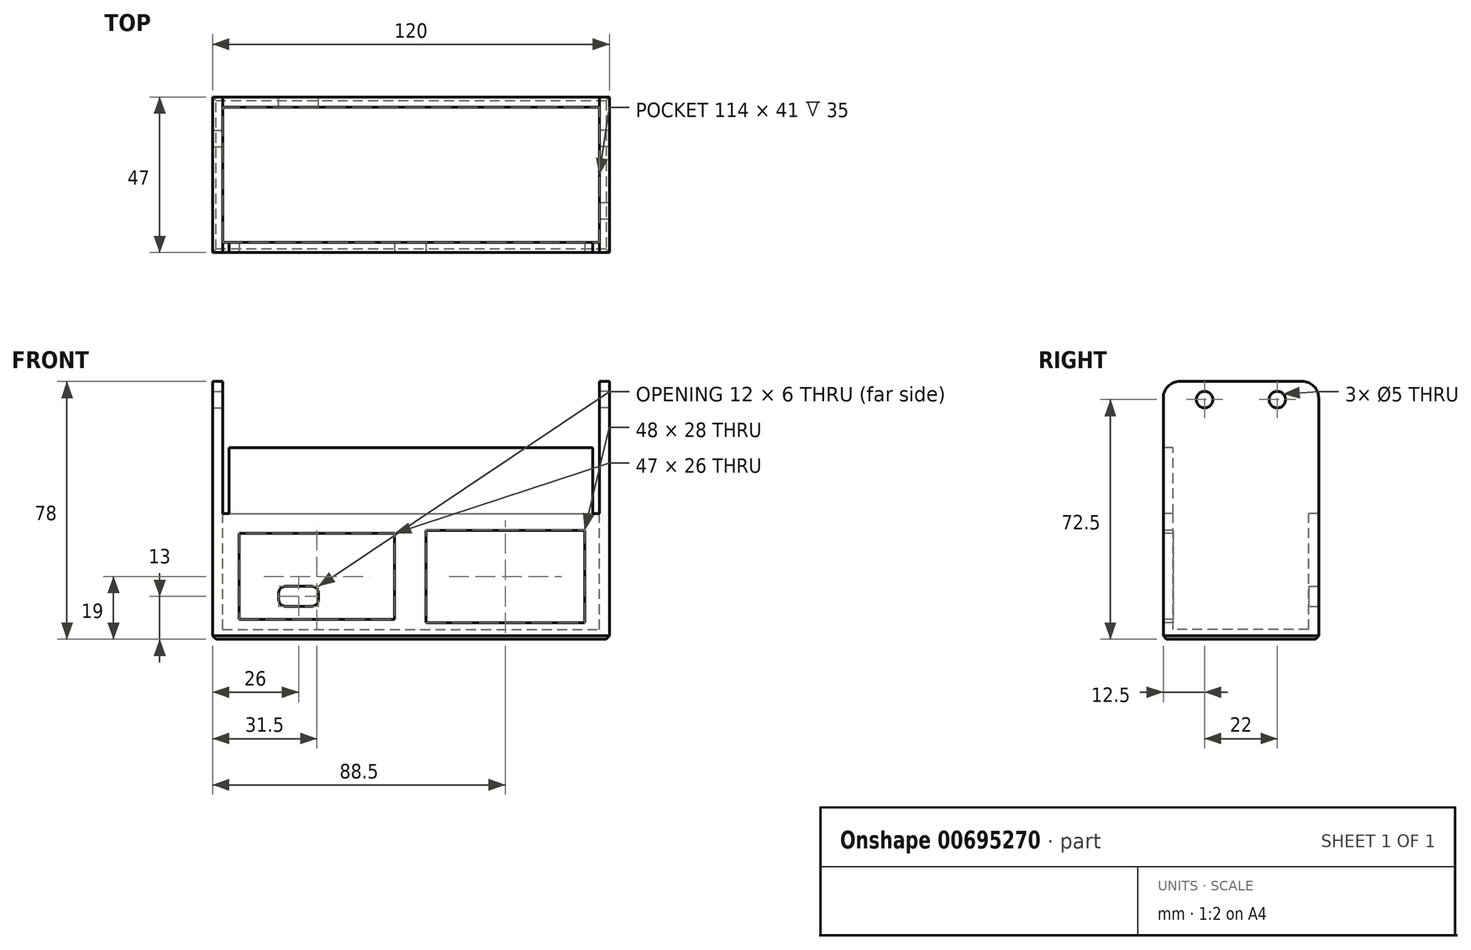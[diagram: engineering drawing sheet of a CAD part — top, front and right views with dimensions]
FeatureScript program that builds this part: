
annotation { "Feature Type Name" : "Feature", "Feature Type Description" : "" }
export const myFeature = defineFeature(function(context is Context, id is Id, definition is map)
    precondition{}
    {
        {
            assignVariable(context, id + "F0", {"name" : "wall", "anyValue" : 3});
        }
        {
            assignVariable(context, id + "F1", {"name" : "width", "anyValue" : 114});
        }
        {
            var Q0;
            Q0=qCreatedBy(makeId("Right.planeOp"),FACE);
            var sketch = newSketch(context, id + "F2", { "sketchPlane" : qUnion([Q0])});
            skLineSegment(sketch, "E0.bottom", {"start": v(17.5, 40) * mm, "end": v(-19.5, 40) * mm});
            skLineSegment(sketch, "E0.top", {"start": v(22.5, -38) * mm, "end": v(-24.5, -38) * mm});
            skLineSegment(sketch, "E0.left", {"start": v(22.5, 35) * mm, "end": v(22.5, -38) * mm});
            skLineSegment(sketch, "E0.right", {"start": v(-24.5, 35) * mm, "end": v(-24.5, -38) * mm});
            skCircle(sketch, "E1", {"center": v(10, 34.5) * mm, "radius": 2.5 * mm});
            skCircle(sketch, "E2", {"center": v(-12, 34.5) * mm, "radius": 2.5 * mm});
            skPoint(sketch, "E3.visualSharp", {"position": v(-24.5, 40) * mm});
            skArc(sketch, "E3.filletArc", {"start": v(-19.5, 40) * mm, "mid": v(-23.04, 38.54) * mm, "end": v(-24.5, 35) * mm});
            skPoint(sketch, "E4.visualSharp", {"position": v(22.5, 40) * mm});
            skArc(sketch, "E4.filletArc", {"start": v(22.5, 35) * mm, "mid": v(21.04, 38.54) * mm, "end": v(17.5, 40) * mm});
            skSolve(sketch);
        }
        {
            var Q0;
            Q0=qSketchRegion(id+"F2",true);
            extrude(context, id + "F3", {"entities" : qUnion([Q0]), "depth" : (getVariable(context, 'wall')) * mm, "offsetDistance" : 25 * mm});
        }
        {
            var Q0;
            Q0=qCreatedBy(makeId("Right.planeOp"),FACE);
            var sketch = newSketch(context, id + "F4", { "sketchPlane" : qUnion([Q0])});
            skLineSegment(sketch, "E5.bottom", {"start": v(22.5, -38) * mm, "end": v(-24.5, -38) * mm});
            skLineSegment(sketch, "E5.top", {"start": v(22.5, -35) * mm, "end": v(-24.5, -35) * mm});
            skLineSegment(sketch, "E5.left", {"start": v(22.5, -38) * mm, "end": v(22.5, -35) * mm});
            skLineSegment(sketch, "E5.right", {"start": v(-24.5, -38) * mm, "end": v(-24.5, -35) * mm});
            skLineSegment(sketch, "E6.bottom", {"start": v(-24.5, -38) * mm, "end": v(-21.5, -38) * mm});
            skLineSegment(sketch, "E6.top", {"start": v(-24.5, 0) * mm, "end": v(-21.5, 0) * mm});
            skLineSegment(sketch, "E6.left", {"start": v(-24.5, -38) * mm, "end": v(-24.5, 0) * mm});
            skLineSegment(sketch, "E6.right", {"start": v(-21.5, -38) * mm, "end": v(-21.5, 0) * mm});
            skLineSegment(sketch, "E7.bottom", {"start": v(22.5, -38) * mm, "end": v(19.5, -38) * mm});
            skLineSegment(sketch, "E7.top", {"start": v(22.5, 0) * mm, "end": v(19.5, 0) * mm});
            skLineSegment(sketch, "E7.left", {"start": v(22.5, -38) * mm, "end": v(22.5, 0) * mm});
            skLineSegment(sketch, "E7.right", {"start": v(19.5, -38) * mm, "end": v(19.5, 0) * mm});
            skSolve(sketch);
        }
        {
            var Q0;
            Q0=qSketchRegion(id+"F4",true);
            extrude(context, id + "F5", {"entities" : qUnion([Q0]), "operationType" : NewBodyOperationType.ADD, "oppositeDirection" : true, "depth" : (getVariable(context, 'width')) * mm, "offsetDistance" : 25 * mm});
        }
        {
            var Q0;
            Q0=makeQuery(id+"F5.opExtrude","CAP_FACE",FACE,{"disambiguationData":[OSD([sQuery(id+"F4.wireOp",EDGE,"E5.bottom"),sQuery(id+"F4.wireOp",EDGE,"E5.top"),sQuery(id+"F4.wireOp",EDGE,"E6.bottom"),sQuery(id+"F4.wireOp",EDGE,"E6.top"),sQuery(id+"F4.wireOp",EDGE,"E6.left"),sQuery(id+"F4.wireOp",EDGE,"E6.right"),sQuery(id+"F4.wireOp",EDGE,"E7.bottom"),sQuery(id+"F4.wireOp",EDGE,"E7.top"),sQuery(id+"F4.wireOp",EDGE,"E7.left"),sQuery(id+"F4.wireOp",EDGE,"E7.right")])],"isStart":false});
            var sketch = newSketch(context, id + "F6", { "sketchPlane" : qUnion([Q0])});
            skLineSegment(sketch, "E8.bottom", {"start": v(19.5, 40) * mm, "end": v(-17.5, 40) * mm});
            skLineSegment(sketch, "E8.top", {"start": v(24.5, -38) * mm, "end": v(-22.5, -38) * mm});
            skLineSegment(sketch, "E8.left", {"start": v(24.5, 35) * mm, "end": v(24.5, -38) * mm});
            skLineSegment(sketch, "E8.right", {"start": v(-22.5, 35) * mm, "end": v(-22.5, -38) * mm});
            skCircle(sketch, "E9", {"center": v(-10, 34.5) * mm, "radius": 2.5 * mm});
            skPoint(sketch, "E10.visualSharp", {"position": v(-22.5, 40) * mm});
            skArc(sketch, "E10.filletArc", {"start": v(-17.5, 40) * mm, "mid": v(-21.04, 38.54) * mm, "end": v(-22.5, 35) * mm});
            skPoint(sketch, "E11.visualSharp", {"position": v(24.5, 40) * mm});
            skArc(sketch, "E11.filletArc", {"start": v(24.5, 35) * mm, "mid": v(23.04, 38.54) * mm, "end": v(19.5, 40) * mm});
            skSolve(sketch);
        }
        {
            var Q0;
            Q0=qSketchRegion(id+"F6",true);
            extrude(context, id + "F7", {"entities" : qUnion([Q0]), "operationType" : NewBodyOperationType.ADD, "depth" : (getVariable(context, 'wall')) * mm, "offsetDistance" : 25 * mm});
        }
        {
            var Q0;
            Q0=makeQuery(id+"F7.boolean.opBoolean","MERGE",FACE,{"derivedFrom":[makeQuery(id+"F5.boolean.opBoolean","MERGE",FACE,{"derivedFrom":[makeQuery(id+"F3.opExtrude","SWEPT_FACE",FACE,{"disambiguationData":[OSD([sQuery(id+"F2.wireOp",EDGE,"E0.right")])]}),makeQuery(id+"F5.opExtrude","SWEPT_FACE",FACE,{"disambiguationData":[OSD([sQuery(id+"F4.wireOp",EDGE,"E6.left")])]})]}),makeQuery(id+"F7.opExtrude","SWEPT_FACE",FACE,{"disambiguationData":[OSD([sQuery(id+"F6.wireOp",EDGE,"E8.left")])]})]});
            var sketch = newSketch(context, id + "F8", { "sketchPlane" : qUnion([Q0])});
            skLineSegment(sketch, "E12.bottom", {"start": v(-112, 0) * mm, "end": v(-2, 0) * mm});
            skLineSegment(sketch, "E12.top", {"start": v(-112, 20) * mm, "end": v(-2, 20) * mm});
            skLineSegment(sketch, "E12.left", {"start": v(-112, 0) * mm, "end": v(-112, 20) * mm});
            skLineSegment(sketch, "E12.right", {"start": v(-2, 0) * mm, "end": v(-2, 20) * mm});
            skSolve(sketch);
        }
        {
            var Q0;
            Q0=qSketchRegion(id+"F8",true);
            extrude(context, id + "F9", {"entities" : qUnion([Q0]), "operationType" : NewBodyOperationType.ADD, "oppositeDirection" : true, "depth" : (getVariable(context, 'wall')) * mm, "offsetDistance" : 25 * mm});
        }
        {
            var Q0;
            {var subQ2=sQuery(id+"F8.wireOp",EDGE,"E12.bottom");Q0=makeQuery(id+"F8.imprint","IMPRINT",FACE,{"disambiguationData":[TD([[makeQuery(id+"F8.imprint","IMPRINT",EDGE,{"derivedFrom":subQ2}),-1.0]])]});}
            var sketch = newSketch(context, id + "F10", { "sketchPlane" : qUnion([Q0])});
            skLineSegment(sketch, "E13.bottom", {"start": v(-109, -6) * mm, "end": v(-62, -6) * mm});
            skLineSegment(sketch, "E13.top", {"start": v(-109, -32) * mm, "end": v(-62, -32) * mm});
            skLineSegment(sketch, "E13.left", {"start": v(-109, -6) * mm, "end": v(-109, -32) * mm});
            skLineSegment(sketch, "E13.right", {"start": v(-62, -6) * mm, "end": v(-62, -32) * mm});
            skLineSegment(sketch, "E14.bottom", {"start": v(-52.5, -5) * mm, "end": v(-4.5, -5) * mm});
            skLineSegment(sketch, "E14.top", {"start": v(-52.5, -33) * mm, "end": v(-4.5, -33) * mm});
            skLineSegment(sketch, "E14.left", {"start": v(-52.5, -5) * mm, "end": v(-52.5, -33) * mm});
            skLineSegment(sketch, "E14.right", {"start": v(-4.5, -5) * mm, "end": v(-4.5, -33) * mm});
            skLineSegment(sketch, "E15", {"start": v(-57, 0) * mm, "end": v(-57, -48.8) * mm, "construction": true});
            skLineSegment(sketch, "E16", {"start": v(-121.46, -19) * mm, "end": v(11.47, -19) * mm, "construction": true});
            skSolve(sketch);
        }
        {
            var Q0;
            Q0=qSketchRegion(id+"F10",true);
            extrude(context, id + "F11", {"entities" : qUnion([Q0]), "operationType" : NewBodyOperationType.REMOVE, "endBound" : BoundingType.UP_TO_NEXT, "oppositeDirection" : true, "depth" : 25 * mm, "offsetDistance" : 25 * mm});
        }
        {
            var Q0;
            Q0=makeQuery(id+"F7.boolean.opBoolean","MERGE",FACE,{"derivedFrom":[makeQuery(id+"F5.boolean.opBoolean","MERGE",FACE,{"derivedFrom":[makeQuery(id+"F3.opExtrude","SWEPT_FACE",FACE,{"disambiguationData":[OSD([sQuery(id+"F2.wireOp",EDGE,"E0.left")])]}),makeQuery(id+"F5.opExtrude","SWEPT_FACE",FACE,{"disambiguationData":[OSD([sQuery(id+"F4.wireOp",EDGE,"E7.left")])]})]}),makeQuery(id+"F7.opExtrude","SWEPT_FACE",FACE,{"disambiguationData":[OSD([sQuery(id+"F6.wireOp",EDGE,"E8.right")])]})]});
            var sketch = newSketch(context, id + "F12", { "sketchPlane" : qUnion([Q0])});
            skLineSegment(sketch, "E17.bottom", {"start": v(87, -28) * mm, "end": v(95, -28) * mm});
            skLineSegment(sketch, "E17.top", {"start": v(87, -22) * mm, "end": v(95, -22) * mm});
            skLineSegment(sketch, "E17.left", {"start": v(85, -26) * mm, "end": v(85, -24) * mm});
            skLineSegment(sketch, "E17.right", {"start": v(97, -26) * mm, "end": v(97, -24) * mm});
            skPoint(sketch, "E18.visualSharp", {"position": v(85, -28) * mm});
            skArc(sketch, "E18.filletArc", {"start": v(85, -26) * mm, "mid": v(85.59, -27.41) * mm, "end": v(87, -28) * mm});
            skPoint(sketch, "E19.visualSharp", {"position": v(85, -22) * mm});
            skArc(sketch, "E19.filletArc", {"start": v(87, -22) * mm, "mid": v(85.59, -22.59) * mm, "end": v(85, -24) * mm});
            skPoint(sketch, "E20.visualSharp", {"position": v(97, -22) * mm});
            skArc(sketch, "E20.filletArc", {"start": v(97, -24) * mm, "mid": v(96.41, -22.59) * mm, "end": v(95, -22) * mm});
            skPoint(sketch, "E21.visualSharp", {"position": v(97, -28) * mm});
            skArc(sketch, "E21.filletArc", {"start": v(95, -28) * mm, "mid": v(96.41, -27.41) * mm, "end": v(97, -26) * mm});
            skSolve(sketch);
        }
        {
            var Q0;
            Q0=qSketchRegion(id+"F12",true);
            extrude(context, id + "F13", {"entities" : qUnion([Q0]), "operationType" : NewBodyOperationType.REMOVE, "endBound" : BoundingType.UP_TO_NEXT, "oppositeDirection" : true, "depth" : 25 * mm, "offsetDistance" : 25 * mm});
        }
        {
            var Q0;
            Q0=makeQuery(id+"F7.boolean.opBoolean","MERGE",FACE,{"derivedFrom":[makeQuery(id+"F5.boolean.opBoolean","MERGE",FACE,{"derivedFrom":[makeQuery(id+"F3.opExtrude","SWEPT_FACE",FACE,{"disambiguationData":[OSD([sQuery(id+"F2.wireOp",EDGE,"E0.top")])]}),makeQuery(id+"F5.opExtrude","SWEPT_FACE",FACE,{"disambiguationData":[OSD([sQuery(id+"F4.wireOp",EDGE,"E5.bottom"),sQuery(id+"F4.wireOp",EDGE,"E6.bottom"),sQuery(id+"F4.wireOp",EDGE,"E7.bottom")])]})]}),makeQuery(id+"F7.opExtrude","SWEPT_FACE",FACE,{"disambiguationData":[OSD([sQuery(id+"F6.wireOp",EDGE,"E8.top")])]})]});
            chamfer(context, id + "F14", {"entities" : qUnion([Q0]), "width" : 1 * mm, "tangentPropagation" : true});
        }
    });
